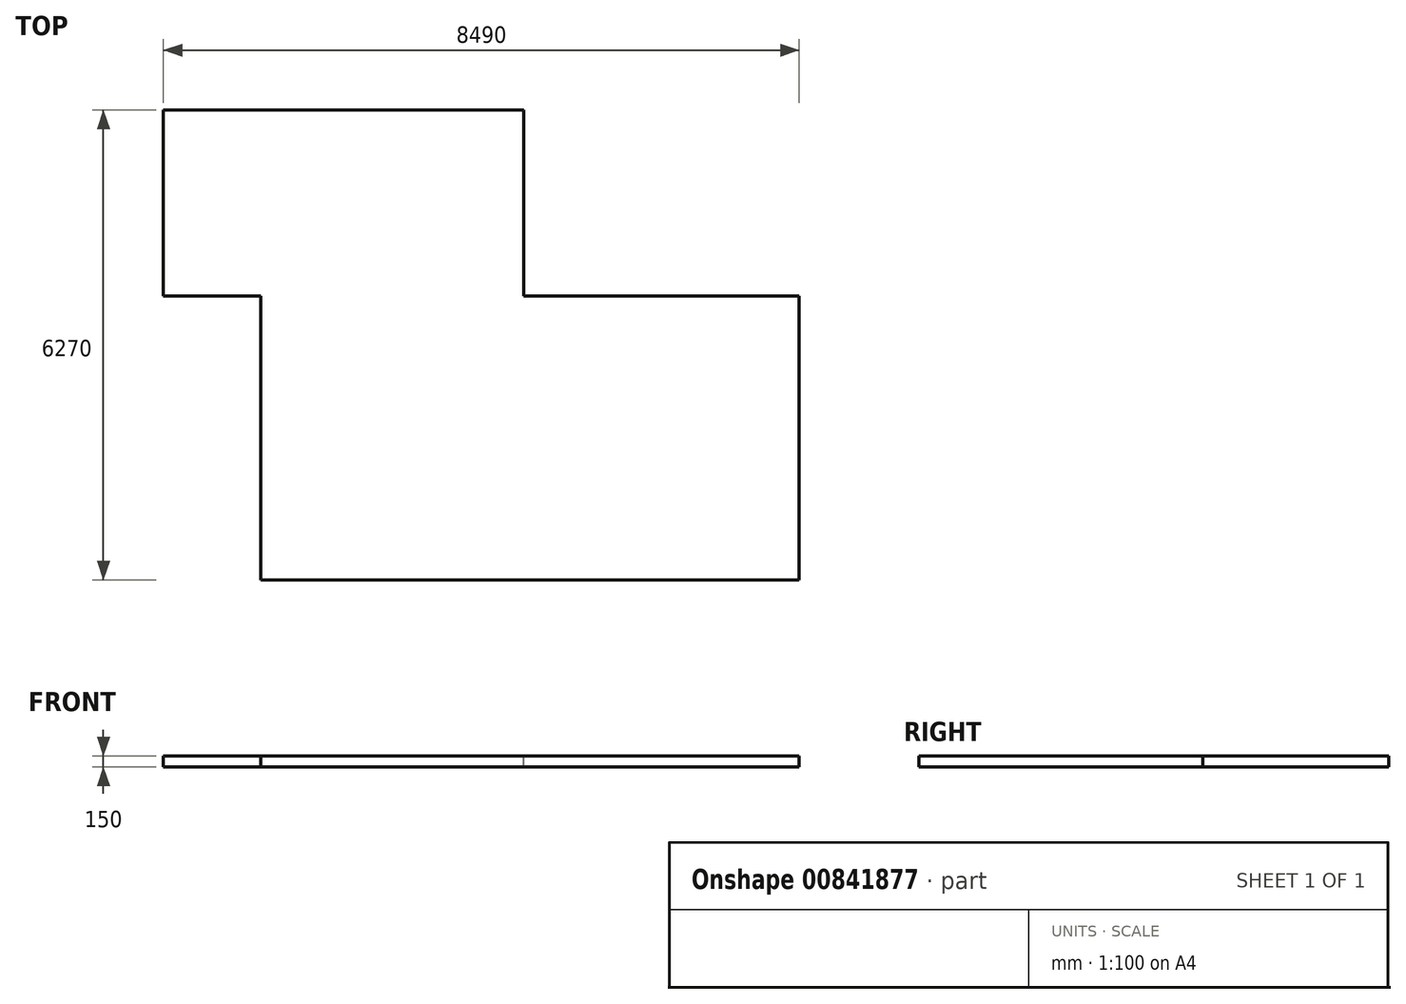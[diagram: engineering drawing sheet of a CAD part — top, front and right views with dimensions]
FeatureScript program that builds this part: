
annotation { "Feature Type Name" : "Feature", "Feature Type Description" : "" }
export const myFeature = defineFeature(function(context is Context, id is Id, definition is map)
    precondition{}
    {
        {
            var Q0;
            Q0=qCreatedBy(makeId("Top.planeOp"),FACE);
            var sketch = newSketch(context, id + "F0", { "sketchPlane" : qUnion([Q0])});
            skLineSegment(sketch, "E0.bottom", {"start": v(0, 0) * mm, "end": v(7190, 0) * mm});
            skLineSegment(sketch, "E0.top", {"start": v(0, 6270) * mm, "end": v(7190, 6270) * mm});
            skLineSegment(sketch, "E0.left", {"start": v(0, 0) * mm, "end": v(0, 3790) * mm});
            skLineSegment(sketch, "E0.right", {"start": v(7190, 0) * mm, "end": v(7190, 6270) * mm});
            skLineSegment(sketch, "E1.bottom", {"start": v(0, 6270) * mm, "end": v(-1300, 6270) * mm});
            skLineSegment(sketch, "E1.top", {"start": v(0, 3790) * mm, "end": v(-1300, 3790) * mm});
            skLineSegment(sketch, "E1.right", {"start": v(-1300, 6270) * mm, "end": v(-1300, 3790) * mm});
            skLineSegment(sketch, "E2.bottom", {"start": v(-1300, 6270) * mm, "end": v(7190, 6270) * mm});
            skLineSegment(sketch, "E2.top", {"start": v(-1300, 7560) * mm, "end": v(7190, 7560) * mm});
            skLineSegment(sketch, "E2.left", {"start": v(-1300, 6270) * mm, "end": v(-1300, 7560) * mm});
            skLineSegment(sketch, "E2.right", {"start": v(7190, 6270) * mm, "end": v(7190, 7560) * mm});
            skLineSegment(sketch, "E3.bottom", {"start": v(7190, 6270) * mm, "end": v(3510, 6270) * mm});
            skLineSegment(sketch, "E3.top", {"start": v(7190, 3790) * mm, "end": v(3510, 3790) * mm});
            skLineSegment(sketch, "E3.left", {"start": v(7190, 6270) * mm, "end": v(7190, 3790) * mm});
            skLineSegment(sketch, "E3.right", {"start": v(3510, 6270) * mm, "end": v(3510, 3790) * mm});
            skSolve(sketch);
        }
        {
            var Q0;
            Q0=makeQuery(id+"F0.imprint","IMPRINT",FACE,{"disambiguationData":[TD([[makeQuery(id+"F0.imprint","IMPRINT",EDGE,{"derivedFrom":sQuery(id+"F0.wireOp",EDGE,"E0.bottom")}),1.0]])]});
            var Q1;
            Q1=makeQuery(id+"F0.imprint","IMPRINT",FACE,{"disambiguationData":[TD([[makeQuery(id+"F0.imprint","IMPRINT",EDGE,{"derivedFrom":sQuery(id+"F0.wireOp",EDGE,"E3.bottom")}),1.0]])]});
            var Q2;
            Q2=makeQuery(id+"F0.imprint","IMPRINT",FACE,{"disambiguationData":[TD([[makeQuery(id+"F0.imprint","IMPRINT",EDGE,{"derivedFrom":sQuery(id+"F0.wireOp",EDGE,"E2.bottom")}),1.0]])]});
            extrude(context, id + "F1", {"entities" : qUnion([Q0, Q1, Q2]), "oppositeDirection" : true, "depth" : 150 * mm, "offsetDistance" : 25 * mm});
        }
    });
